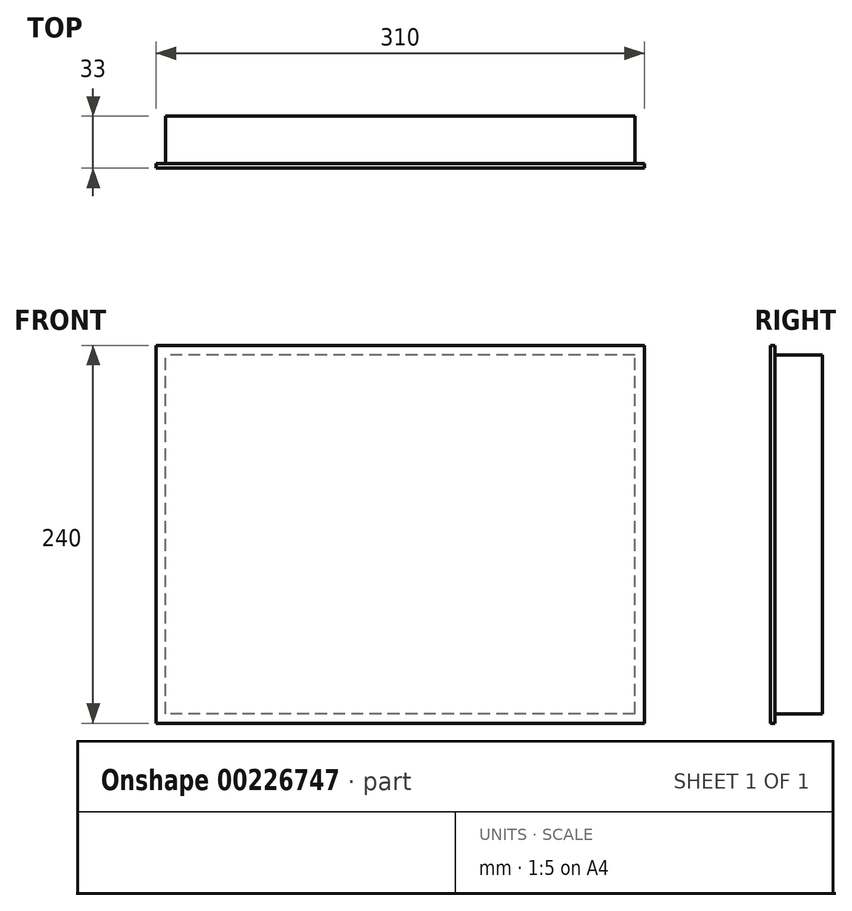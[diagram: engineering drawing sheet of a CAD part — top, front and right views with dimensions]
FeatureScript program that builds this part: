
annotation { "Feature Type Name" : "Feature", "Feature Type Description" : "" }
export const myFeature = defineFeature(function(context is Context, id is Id, definition is map)
    precondition{}
    {
        {
            var Q0;
            Q0=qCreatedBy(makeId("Front.planeOp"),FACE);
            var sketch = newSketch(context, id + "F0", { "sketchPlane" : qUnion([Q0])});
            skLineSegment(sketch, "E0.bottom", {"start": v(155, -120) * mm, "end": v(-155, -120) * mm});
            skLineSegment(sketch, "E0.top", {"start": v(155, 120) * mm, "end": v(-155, 120) * mm});
            skLineSegment(sketch, "E0.left", {"start": v(155, -120) * mm, "end": v(155, 120) * mm});
            skLineSegment(sketch, "E0.right", {"start": v(-155, -120) * mm, "end": v(-155, 120) * mm});
            skPoint(sketch, "E0.middle", {"position": v(0, 0) * mm});
            skSolve(sketch);
        }
        {
            var Q0;
            Q0=makeQuery(id+"F0.imprint","IMPRINT",FACE,{"disambiguationData":[TD([[makeQuery(id+"F0.imprint","IMPRINT",EDGE,{"derivedFrom":sQuery(id+"F0.wireOp",EDGE,"E0.bottom")}),-1.0]])]});
            var sketch = newSketch(context, id + "F1", { "sketchPlane" : qUnion([Q0])});
            skLineSegment(sketch, "E1.0", {"start": v(-149, -114) * mm, "end": v(-149, 114) * mm});
            skLineSegment(sketch, "E1.1", {"start": v(149, -114) * mm, "end": v(-149, -114) * mm});
            skLineSegment(sketch, "E1.2", {"start": v(149, -114) * mm, "end": v(149, 114) * mm});
            skLineSegment(sketch, "E1.3", {"start": v(149, 114) * mm, "end": v(-149, 114) * mm});
            skSolve(sketch);
        }
        {
            var Q0;
            Q0=makeQuery(id+"F1.imprint","IMPRINT",FACE,{"disambiguationData":[TD([[makeQuery(id+"F1.imprint","IMPRINT",EDGE,{"derivedFrom":sQuery(id+"F1.wireOp",EDGE,"E1.0")}),-1.0]])]});
            extrude(context, id + "F2", {"entities" : qUnion([Q0]), "oppositeDirection" : true, "depth" : 30 * mm});
        }
        {
            var Q0;
            Q0=makeQuery(id+"F0.imprint","IMPRINT",FACE,{"disambiguationData":[TD([[makeQuery(id+"F0.imprint","IMPRINT",EDGE,{"derivedFrom":sQuery(id+"F0.wireOp",EDGE,"E0.bottom")}),-1.0]])]});
            extrude(context, id + "F3", {"entities" : qUnion([Q0]), "operationType" : NewBodyOperationType.ADD, "depth" : 3 * mm});
        }
    });
